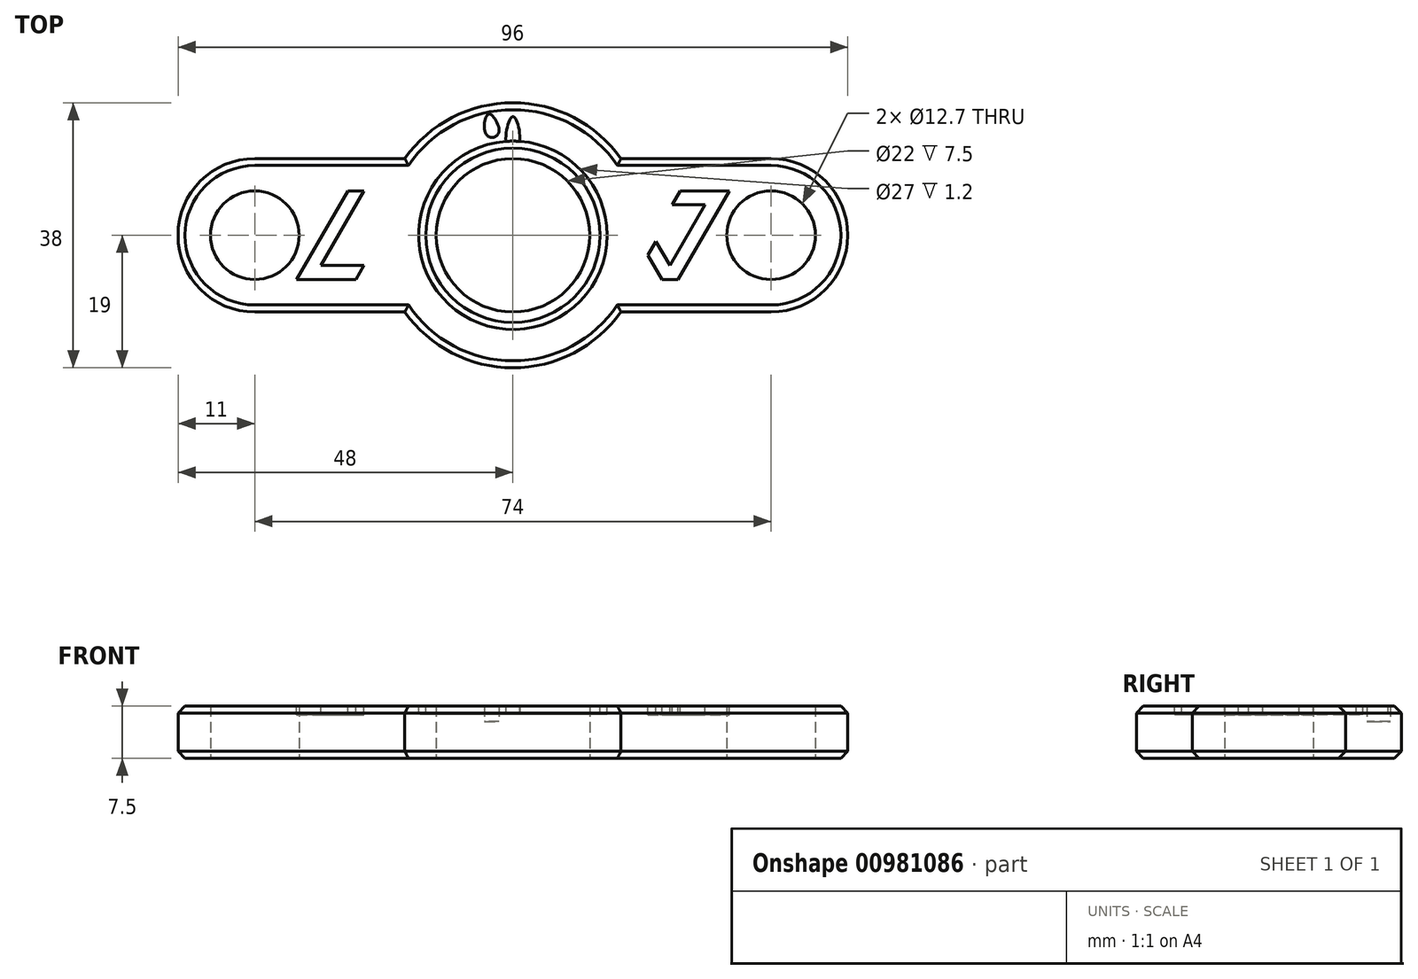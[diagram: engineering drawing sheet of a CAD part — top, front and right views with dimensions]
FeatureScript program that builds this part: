
annotation { "Feature Type Name" : "Feature", "Feature Type Description" : "" }
export const myFeature = defineFeature(function(context is Context, id is Id, definition is map)
    precondition{}
    {
        {
            var Q0;
            Q0=qCreatedBy(makeId("Top.planeOp"),FACE);
            var sketch = newSketch(context, id + "F0", { "sketchPlane" : qUnion([Q0])});
            skCircle(sketch, "E0", {"center": v(0, 0) * mm, "radius": 11 * mm});
            skCircle(sketch, "E1", {"center": v(0, 0) * mm, "radius": 19 * mm});
            skLineSegment(sketch, "E2", {"start": v(0, 0) * mm, "end": v(0, 11) * mm, "construction": true});
            skLineSegment(sketch, "E3", {"start": v(0, 0) * mm, "end": v(0, -11) * mm, "construction": true});
            skLineSegment(sketch, "E4", {"start": v(0, -11) * mm, "end": v(37, -11) * mm});
            skLineSegment(sketch, "E5", {"start": v(0, 11) * mm, "end": v(37, 11) * mm});
            skLineSegment(sketch, "E6", {"start": v(37, 11) * mm, "end": v(37, -11) * mm, "construction": true});
            skLineSegment(sketch, "E7", {"start": v(0, -11) * mm, "end": v(-37, -11) * mm});
            skLineSegment(sketch, "E8", {"start": v(-37, -11) * mm, "end": v(-37, 11) * mm, "construction": true});
            skLineSegment(sketch, "E9", {"start": v(-37, 11) * mm, "end": v(0, 11) * mm});
            skCircle(sketch, "E10", {"center": v(-37, 0) * mm, "radius": 11 * mm});
            skCircle(sketch, "E11", {"center": v(37, 0) * mm, "radius": 11 * mm});
            skCircle(sketch, "E12", {"center": v(-37, 0) * mm, "radius": 6.35 * mm});
            skCircle(sketch, "E13", {"center": v(37, 0) * mm, "radius": 6.35 * mm});
            skSolve(sketch);
        }
        {
            var Q0;
            Q0 = qSketchRegion(id + "F0", true);
            extrude(context, id + "F1", {"entities" : qUnion([Q0]), "depth" : 7.5 * mm, "offsetDistance" : 25 * mm});
        }
        {
            var Q0;
            Q0=makeQuery(id+"F1.opExtrude","CAP_FACE",FACE,{"disambiguationData":[OSD([sQuery(id+"F0.wireOp",EDGE,"E0"),sQuery(id+"F0.wireOp",EDGE,"E1"),sQuery(id+"F0.wireOp",EDGE,"E4"),sQuery(id+"F0.wireOp",EDGE,"E5"),sQuery(id+"F0.wireOp",EDGE,"E7"),sQuery(id+"F0.wireOp",EDGE,"E9"),sQuery(id+"F0.wireOp",EDGE,"E10"),sQuery(id+"F0.wireOp",EDGE,"E11"),sQuery(id+"F0.wireOp",EDGE,"E12"),sQuery(id+"F0.wireOp",EDGE,"E13")])],"isStart":false});
            var sketch = newSketch(context, id + "F2", { "sketchPlane" : qUnion([Q0])});
            skLineSegment(sketch, "E14", {"start": v(-37, 0) * mm, "end": v(-37, -6.35) * mm, "construction": true});
            skLineSegment(sketch, "E15", {"start": v(-37, -6.35) * mm, "end": v(37, -6.35) * mm, "construction": true});
            skLineSegment(sketch, "E16", {"start": v(37, -6.35) * mm, "end": v(37, 0) * mm, "construction": true});
            skLineSegment(sketch, "E17", {"start": v(37, 0) * mm, "end": v(37, 6.35) * mm, "construction": true});
            skLineSegment(sketch, "E18", {"start": v(37, 6.35) * mm, "end": v(-37, 6.35) * mm, "construction": true});
            skLineSegment(sketch, "E19", {"start": v(-37, 6.35) * mm, "end": v(-37, 0) * mm, "construction": true});
            skLineSegment(sketch, "E20", {"start": v(-23.67, 6.35) * mm, "end": v(-31, -6.35) * mm});
            skLineSegment(sketch, "E21", {"start": v(-31, -6.35) * mm, "end": v(-22.5, -6.35) * mm});
            skLineSegment(sketch, "E22", {"start": v(-22.5, -6.35) * mm, "end": v(-21.35, -4.35) * mm});
            skLineSegment(sketch, "E23", {"start": v(-21.35, -4.35) * mm, "end": v(-27.54, -4.35) * mm});
            skLineSegment(sketch, "E24", {"start": v(-27.54, -4.35) * mm, "end": v(-21.36, 6.35) * mm});
            skLineSegment(sketch, "E25", {"start": v(-21.36, 6.35) * mm, "end": v(-23.67, 6.35) * mm});
            skLineSegment(sketch, "E26", {"start": v(24, 6.35) * mm, "end": v(22.85, 4.35) * mm});
            skLineSegment(sketch, "E27", {"start": v(22.85, 4.35) * mm, "end": v(27.54, 4.35) * mm});
            skLineSegment(sketch, "E28", {"start": v(27.54, 4.35) * mm, "end": v(21.36, -6.35) * mm});
            skLineSegment(sketch, "E29", {"start": v(21.36, -6.35) * mm, "end": v(23.67, -6.35) * mm});
            skLineSegment(sketch, "E30", {"start": v(23.67, -6.35) * mm, "end": v(31, 6.35) * mm});
            skLineSegment(sketch, "E31", {"start": v(31, 6.35) * mm, "end": v(24, 6.35) * mm});
            skLineSegment(sketch, "E32", {"start": v(22.51, -4.35) * mm, "end": v(20.51, -0.89) * mm});
            skLineSegment(sketch, "E33", {"start": v(20.51, -0.89) * mm, "end": v(19.36, -2.89) * mm});
            skLineSegment(sketch, "E34", {"start": v(19.36, -2.89) * mm, "end": v(21.36, -6.35) * mm});
            skSolve(sketch);
        }
        {
            var Q0;
            Q0=makeQuery(id+"F2.imprint","IMPRINT",FACE,{"disambiguationData":[TD([[makeQuery(id+"F2.imprint","IMPRINT",EDGE,{"derivedFrom":sQuery(id+"F2.wireOp",EDGE,"E20")}),1.0]])]});
            var Q1;
            Q1=makeQuery(id+"F2.imprint","IMPRINT",FACE,{"disambiguationData":[TD([[makeQuery(id+"F2.imprint","IMPRINT",EDGE,{"derivedFrom":sQuery(id+"F2.wireOp",EDGE,"E26")}),1.0]])]});
            var Q2;
            {var subQ2=sQuery(id+"F2.wireOp",EDGE,"E32");Q2=makeQuery(id+"F2.imprint","IMPRINT",FACE,{"disambiguationData":[TD([[makeQuery(id+"F2.imprint","IMPRINT",EDGE,{"derivedFrom":subQ2}),1.0]])]});}
            extrude(context, id + "F3", {"entities" : qUnion([Q0, Q1, Q2]), "operationType" : NewBodyOperationType.REMOVE, "oppositeDirection" : true, "depth" : 1.3 * mm, "offsetDistance" : 25 * mm});
        }
        {
            var Q0;
            Q0=makeQuery(id+"F1.opExtrude","CAP_FACE",FACE,{"disambiguationData":[OSD([sQuery(id+"F0.wireOp",EDGE,"E0"),sQuery(id+"F0.wireOp",EDGE,"E1"),sQuery(id+"F0.wireOp",EDGE,"E4"),sQuery(id+"F0.wireOp",EDGE,"E5"),sQuery(id+"F0.wireOp",EDGE,"E7"),sQuery(id+"F0.wireOp",EDGE,"E9"),sQuery(id+"F0.wireOp",EDGE,"E10"),sQuery(id+"F0.wireOp",EDGE,"E11"),sQuery(id+"F0.wireOp",EDGE,"E12"),sQuery(id+"F0.wireOp",EDGE,"E13")])],"isStart":false});
            var sketch = newSketch(context, id + "F4", { "sketchPlane" : qUnion([Q0])});
            skCircle(sketch, "E35", {"center": v(0, 0) * mm, "radius": 13.5 * mm});
            skLineSegment(sketch, "E36", {"start": v(0, 0) * mm, "end": v(0, 17) * mm, "construction": true});
            skFitSpline(sketch, "E37", {"points": [v(0, 11.6) * mm, v(-1, 13.46) * mm, v(0, 17) * mm, v(1, 13.46) * mm, v(0, 11.6) * mm]});
            skCircle(sketch, "E38", {"center": v(0, 0) * mm, "radius": 12.5 * mm});
            skSolve(sketch);
        }
        {
            var Q0;
            {var subQ0=sQuery(id+"F4.wireOp",EDGE,"E37");var subQ1=sQuery(id+"F4.wireOp",EDGE,"E35");var subQ2=makeQuery(id+"F4.imprint","INTERSECT",VERTEX,{"disambiguationData":[OD(0.0)],"derivedFrom":[subQ1,subQ0]});Q0=makeQuery(id+"F4.imprint","IMPRINT",FACE,{"disambiguationData":[TD([[makeQuery(id+"F4.imprint","IMPRINT",EDGE,{"disambiguationData":[TD([[subQ2,1.0]])],"derivedFrom":subQ1}),-1.0]])]});}
            extrude(context, id + "F5", {"entities" : qUnion([Q0]), "operationType" : NewBodyOperationType.REMOVE, "oppositeDirection" : true, "depth" : 1 * mm, "offsetDistance" : 25 * mm});
        }
        {
            var Q0;
            Q0=makeQuery(id+"F1.opExtrude","CAP_FACE",FACE,{"disambiguationData":[OSD([sQuery(id+"F0.wireOp",EDGE,"E0"),sQuery(id+"F0.wireOp",EDGE,"E1"),sQuery(id+"F0.wireOp",EDGE,"E4"),sQuery(id+"F0.wireOp",EDGE,"E5"),sQuery(id+"F0.wireOp",EDGE,"E7"),sQuery(id+"F0.wireOp",EDGE,"E9"),sQuery(id+"F0.wireOp",EDGE,"E10"),sQuery(id+"F0.wireOp",EDGE,"E11"),sQuery(id+"F0.wireOp",EDGE,"E12"),sQuery(id+"F0.wireOp",EDGE,"E13")])],"isStart":false});
            var sketch = newSketch(context, id + "F6", { "sketchPlane" : qUnion([Q0])});
            skLineSegment(sketch, "E39", {"start": v(-5.09, 14.5) * mm, "end": v(-0.85, 15.35) * mm, "construction": true});
            skLineSegment(sketch, "E40", {"start": v(-2.97, 14.93) * mm, "end": v(0, 0) * mm, "construction": true});
            skLineSegment(sketch, "E41", {"start": v(-2.97, 14.93) * mm, "end": v(-3.46, 17.38) * mm, "construction": true});
            skFitSpline(sketch, "E42", {"points": [v(-2.8, 14.04) * mm, v(-3.95, 14.73) * mm, v(-3.46, 17.38) * mm, v(-1.99, 15.12) * mm, v(-2.8, 14.04) * mm]});
            skLineSegment(sketch, "E43", {"start": v(-3.95, 14.73) * mm, "end": v(-1.99, 15.12) * mm});
            skSolve(sketch);
        }
        {
            var Q0;
            {var subQ0=sQuery(id+"F6.wireOp",EDGE,"E43");Q0=makeQuery(id+"F6.imprint","IMPRINT",FACE,{"disambiguationData":[TD([[makeQuery(id+"F6.imprint","IMPRINT",EDGE,{"derivedFrom":subQ0}),1.0]])]});}
            var Q1;
            {var subQ0=sQuery(id+"F6.wireOp",EDGE,"E43");Q1=makeQuery(id+"F6.imprint","IMPRINT",FACE,{"disambiguationData":[TD([[makeQuery(id+"F6.imprint","IMPRINT",EDGE,{"derivedFrom":subQ0}),-1.0]])]});}
            extrude(context, id + "F7", {"entities" : qUnion([Q0, Q1]), "operationType" : NewBodyOperationType.REMOVE, "oppositeDirection" : true, "depth" : 2.2 * mm, "offsetDistance" : 25 * mm});
        }
        {
            var Q0;
            {var subQ0=sQuery(id+"F4.wireOp",EDGE,"E37");var subQ1=sQuery(id+"F4.wireOp",EDGE,"E35");var subQ2=makeQuery(id+"F4.imprint","INTERSECT",VERTEX,{"disambiguationData":[OD(0.0)],"derivedFrom":[subQ1,subQ0]});Q0=makeQuery(id+"F4.imprint","IMPRINT",FACE,{"disambiguationData":[TD([[makeQuery(id+"F4.imprint","IMPRINT",EDGE,{"disambiguationData":[TD([[subQ2,-1.0]])],"derivedFrom":subQ1}),1.0]])]});}
            var Q1;
            {var subQ0=sQuery(id+"F4.wireOp",EDGE,"E37");var subQ1=sQuery(id+"F4.wireOp",EDGE,"E35");var subQ2=makeQuery(id+"F4.imprint","INTERSECT",VERTEX,{"disambiguationData":[OD(0.0)],"derivedFrom":[subQ1,subQ0]});Q1=makeQuery(id+"F4.imprint","IMPRINT",FACE,{"disambiguationData":[TD([[makeQuery(id+"F4.imprint","IMPRINT",EDGE,{"disambiguationData":[TD([[subQ2,1.0]])],"derivedFrom":subQ1}),1.0]])]});}
            extrude(context, id + "F8", {"entities" : qUnion([Q0, Q1]), "operationType" : NewBodyOperationType.REMOVE, "oppositeDirection" : true, "depth" : 1.2 * mm, "offsetDistance" : 25 * mm});
        }
        {
            var Q0;
            Q0=makeQuery(id+"F1.opExtrude","CAP_EDGE",EDGE,{"disambiguationData":[OSD([sQuery(id+"F0.wireOp",EDGE,"E7")])],"isStart":false});
            var Q1;
            Q1=makeQuery(id+"F1.opExtrude","CAP_EDGE",EDGE,{"disambiguationData":[OSD([sQuery(id+"F0.wireOp",EDGE,"E9")])],"isStart":true});
            var Q2;
            {var subQ0=sQuery(id+"F0.wireOp",EDGE,"E1");Q2=makeQuery(id+"F1.opExtrude","CAP_EDGE",EDGE,{"disambiguationData":[OSD([subQ0]),TDD([makeQuery(id+"F0.imprint","IMPRINT",EDGE,{"disambiguationData":[TD([[makeQuery(id+"F0.imprint","INTERSECT",VERTEX,{"derivedFrom":[subQ0,sQuery(id+"F0.wireOp",EDGE,"E9")]}),1.0]])],"derivedFrom":subQ0})])],"isStart":true});}
            var Q3;
            {var subQ0=sQuery(id+"F0.wireOp",EDGE,"E1");Q3=makeQuery(id+"F1.opExtrude","CAP_EDGE",EDGE,{"disambiguationData":[OSD([subQ0]),TDD([makeQuery(id+"F0.imprint","IMPRINT",EDGE,{"disambiguationData":[TD([[makeQuery(id+"F0.imprint","INTERSECT",VERTEX,{"derivedFrom":[subQ0,sQuery(id+"F0.wireOp",EDGE,"E9")]}),1.0]])],"derivedFrom":subQ0})])],"isStart":false});}
            var Q4;
            Q4=makeQuery(id+"F1.opExtrude","CAP_EDGE",EDGE,{"disambiguationData":[OSD([sQuery(id+"F0.wireOp",EDGE,"E5")])],"isStart":false});
            var Q5;
            Q5=makeQuery(id+"F1.opExtrude","CAP_EDGE",EDGE,{"disambiguationData":[OSD([sQuery(id+"F0.wireOp",EDGE,"E5")])],"isStart":true});
            var Q6;
            {var subQ0=sQuery(id+"F0.wireOp",EDGE,"E1");Q6=makeQuery(id+"F1.opExtrude","CAP_EDGE",EDGE,{"disambiguationData":[OSD([subQ0]),TDD([makeQuery(id+"F0.imprint","IMPRINT",EDGE,{"disambiguationData":[TD([[makeQuery(id+"F0.imprint","INTERSECT",VERTEX,{"derivedFrom":[subQ0,sQuery(id+"F0.wireOp",EDGE,"E7")]}),-1.0]])],"derivedFrom":subQ0})])],"isStart":true});}
            var Q7;
            {var subQ0=sQuery(id+"F0.wireOp",EDGE,"E1");Q7=makeQuery(id+"F1.opExtrude","CAP_EDGE",EDGE,{"disambiguationData":[OSD([subQ0]),TDD([makeQuery(id+"F0.imprint","IMPRINT",EDGE,{"disambiguationData":[TD([[makeQuery(id+"F0.imprint","INTERSECT",VERTEX,{"derivedFrom":[subQ0,sQuery(id+"F0.wireOp",EDGE,"E7")]}),-1.0]])],"derivedFrom":subQ0})])],"isStart":false});}
            chamfer(context, id + "F9", {"entities" : qUnion([Q0, Q1, Q2, Q3, Q4, Q5, Q6, Q7]), "width" : 1 * mm, "tangentPropagation" : true});
        }
    });
